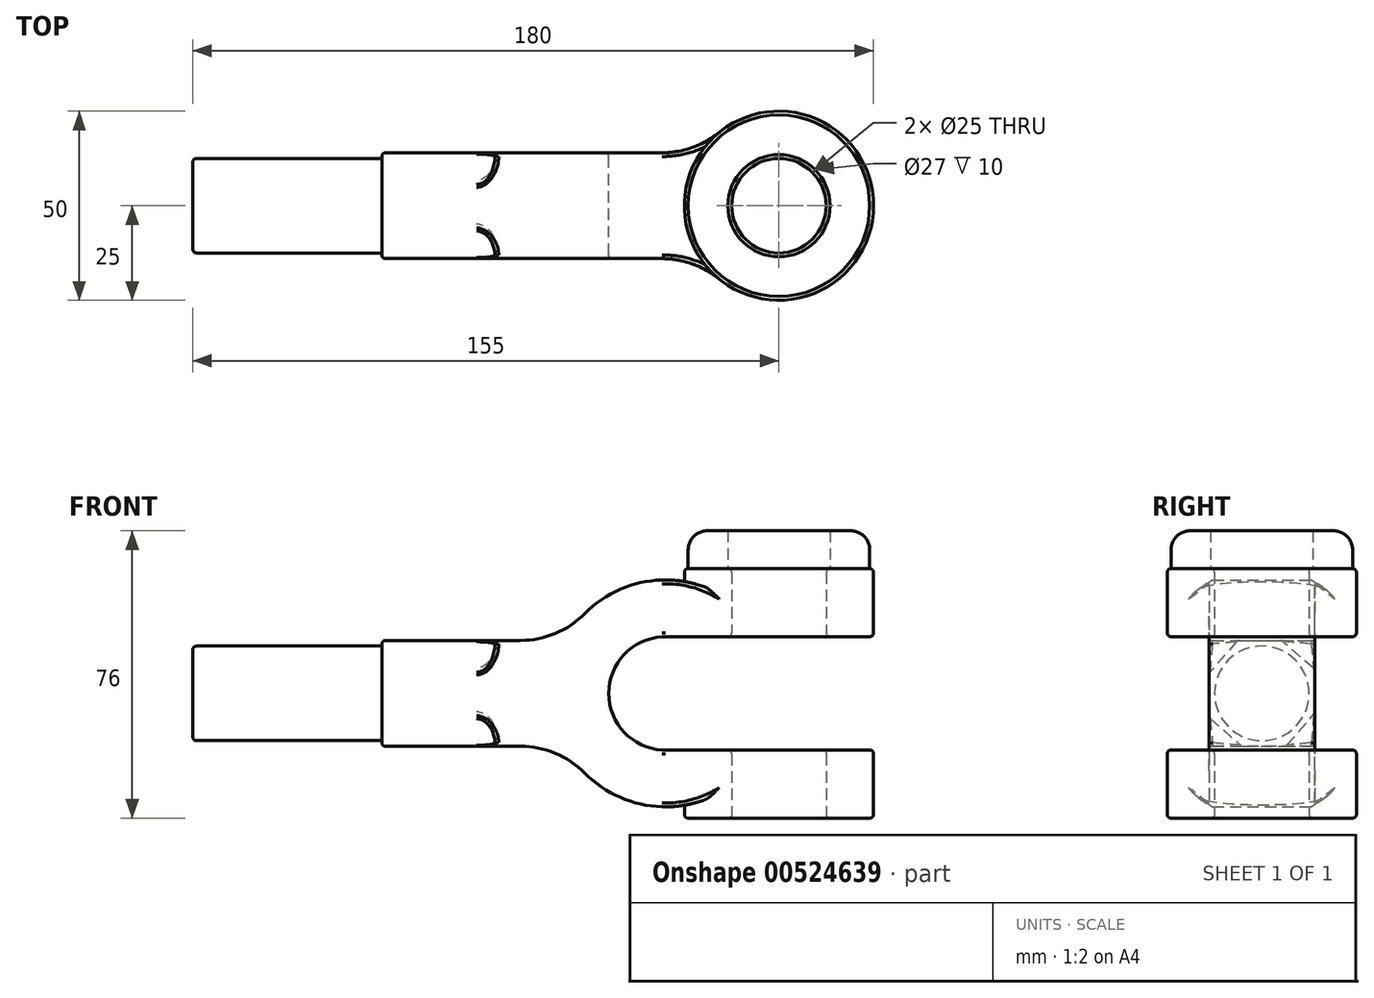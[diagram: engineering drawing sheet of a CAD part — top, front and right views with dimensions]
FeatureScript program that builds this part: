
annotation { "Feature Type Name" : "Feature", "Feature Type Description" : "" }
export const myFeature = defineFeature(function(context is Context, id is Id, definition is map)
    precondition{}
    {
        {
            var Q0;
            Q0=qCreatedBy(makeId("Top.planeOp"),FACE);
            var sketch = newSketch(context, id + "F0", { "sketchPlane" : qUnion([Q0])});
            skCircle(sketch, "E0", {"center": v(0, 0) * mm, "radius": 25 * mm});
            skSolve(sketch);
        }
        {
            var Q0;
            Q0=qSketchRegion(id+"F0",true);
            extrude(context, id + "F1", {"entities" : qUnion([Q0]), "endBound" : BoundingType.SYMMETRIC, "depth" : 66 * mm, "offsetDistance" : 25 * mm});
        }
        {
            var Q0;
            Q0=qCreatedBy(makeId("Front.planeOp"),FACE);
            var sketch = newSketch(context, id + "F2", { "sketchPlane" : qUnion([Q0])});
            skArc(sketch, "E1", {"start": v(-56.53, -14) * mm, "mid": v(0, 0) * mm, "end": v(-56.53, 14) * mm});
            skCircle(sketch, "E2", {"center": v(-30, 0) * mm, "radius": 15 * mm});
            skLineSegment(sketch, "E3.bottom", {"start": v(-75, 14) * mm, "end": v(-65, 14) * mm});
            skLineSegment(sketch, "E3.top", {"start": v(-75, -14) * mm, "end": v(-56.53, -14) * mm});
            skLineSegment(sketch, "E3.left", {"start": v(-75, 14) * mm, "end": v(-75, -14) * mm});
            skLineSegment(sketch, "E4", {"start": v(-65, 14) * mm, "end": v(-56.53, 14) * mm});
            skPoint(sketch, "E5.orphan", {"position": v(-55, 14) * mm});
            skSolve(sketch);
        }
        {
            var Q0;
            Q0=qSketchRegion(id+"F2",true);
            extrude(context, id + "F3", {"entities" : qUnion([Q0]), "operationType" : NewBodyOperationType.ADD, "endBound" : BoundingType.SYMMETRIC, "depth" : 28 * mm, "offsetDistance" : 25 * mm});
        }
        {
            var Q0;
            Q0=makeQuery(id+"F3.opExtrude","SWEPT_FACE",FACE,{"disambiguationData":[OSD([sQuery(id+"F2.wireOp",EDGE,"E3.left")])]});
            extrude(context, id + "F4", {"entities" : qUnion([Q0]), "operationType" : NewBodyOperationType.ADD, "depth" : 30 * mm, "offsetDistance" : 25 * mm});
        }
        {
            var Q0;
            Q0=makeQuery(id+"F4.opExtrude","CAP_FACE",FACE,{"disambiguationData":[OSD([sQuery(id+"F2.wireOp",EDGE,"E3.left")])],"isStart":false});
            var sketch = newSketch(context, id + "F5", { "sketchPlane" : qUnion([Q0])});
            skCircle(sketch, "E6", {"center": v(0, 0) * mm, "radius": 12.5 * mm});
            skSolve(sketch);
        }
        {
            var Q0;
            Q0=qSketchRegion(id+"F5",true);
            extrude(context, id + "F6", {"entities" : qUnion([Q0]), "operationType" : NewBodyOperationType.ADD, "depth" : 50 * mm, "offsetDistance" : 25 * mm});
        }
        {
            var Q0;
            Q0=qCreatedBy(makeId("Front.planeOp"),FACE);
            var sketch = newSketch(context, id + "F7", { "sketchPlane" : qUnion([Q0])});
            skLineSegment(sketch, "E7.bottom", {"start": v(-30, 15) * mm, "end": v(30, 15) * mm});
            skLineSegment(sketch, "E7.top", {"start": v(-30, -15) * mm, "end": v(30, -15) * mm});
            skLineSegment(sketch, "E7.left", {"start": v(-30, 15) * mm, "end": v(-30, -15) * mm});
            skLineSegment(sketch, "E7.right", {"start": v(30, 15) * mm, "end": v(30, -15) * mm});
            skPoint(sketch, "E7.middle", {"position": v(0, 0) * mm});
            skSolve(sketch);
        }
        {
            var Q0;
            Q0=qSketchRegion(id+"F7",true);
            extrude(context, id + "F8", {"entities" : qUnion([Q0]), "operationType" : NewBodyOperationType.REMOVE, "endBound" : BoundingType.SYMMETRIC, "oppositeDirection" : true, "depth" : 60 * mm, "offsetDistance" : 25 * mm});
        }
        {
            var Q0;
            Q0=makeQuery(id+"F1.opExtrude","CAP_FACE",FACE,{"disambiguationData":[OSD([sQuery(id+"F0.wireOp",EDGE,"E0")])],"isStart":true});
            var sketch = newSketch(context, id + "F9", { "sketchPlane" : qUnion([Q0])});
            skCircle(sketch, "E8", {"center": v(0, 0) * mm, "radius": 12.5 * mm});
            skSolve(sketch);
        }
        {
            var Q0;
            Q0=qSketchRegion(id+"F9",true);
            extrude(context, id + "F10", {"entities" : qUnion([Q0]), "operationType" : NewBodyOperationType.REMOVE, "endBound" : BoundingType.THROUGH_ALL, "oppositeDirection" : true, "depth" : 25 * mm, "offsetDistance" : 25 * mm});
        }
        {
            var Q0;
            Q0=makeQuery(id+"F3.boolean.opBoolean","INTERSECT",EDGE,{"disambiguationData":[OD(1.0)],"derivedFrom":[makeQuery(id+"F1.opExtrude","SWEPT_FACE",FACE,{"disambiguationData":[OSD([sQuery(id+"F0.wireOp",EDGE,"E0")])]}),makeQuery(id+"F3.opExtrude","CAP_FACE",FACE,{"disambiguationData":[OSD([sQuery(id+"F2.wireOp",EDGE,"E1"),sQuery(id+"F2.wireOp",EDGE,"E2"),sQuery(id+"F2.wireOp",EDGE,"E3.bottom"),sQuery(id+"F2.wireOp",EDGE,"E3.top"),sQuery(id+"F2.wireOp",EDGE,"E3.left"),sQuery(id+"F2.wireOp",EDGE,"E4")])],"isStart":false})]});
            fillet(context, id + "F11", {"entities" : qUnion([Q0]), "radius" : 24 * mm, "tangentPropagation" : true, "allowEdgeOverflow" : false});
        }
        {
            var Q0;
            Q0=makeQuery(id+"F3.boolean.opBoolean","INTERSECT",EDGE,{"disambiguationData":[OD(0.0)],"derivedFrom":[makeQuery(id+"F1.opExtrude","SWEPT_FACE",FACE,{"disambiguationData":[OSD([sQuery(id+"F0.wireOp",EDGE,"E0")])]}),makeQuery(id+"F3.opExtrude","CAP_FACE",FACE,{"disambiguationData":[OSD([sQuery(id+"F2.wireOp",EDGE,"E1"),sQuery(id+"F2.wireOp",EDGE,"E2"),sQuery(id+"F2.wireOp",EDGE,"E3.bottom"),sQuery(id+"F2.wireOp",EDGE,"E3.top"),sQuery(id+"F2.wireOp",EDGE,"E3.left"),sQuery(id+"F2.wireOp",EDGE,"E4")])],"isStart":false})]});
            fillet(context, id + "F12", {"entities" : qUnion([Q0]), "radius" : 24 * mm, "tangentPropagation" : true, "allowEdgeOverflow" : false});
        }
        {
            var Q0;
            Q0=makeQuery(id+"F3.boolean.opBoolean","INTERSECT",EDGE,{"disambiguationData":[OD(0.0)],"derivedFrom":[makeQuery(id+"F1.opExtrude","SWEPT_FACE",FACE,{"disambiguationData":[OSD([sQuery(id+"F0.wireOp",EDGE,"E0")])]}),makeQuery(id+"F3.opExtrude","CAP_FACE",FACE,{"disambiguationData":[OSD([sQuery(id+"F2.wireOp",EDGE,"E1"),sQuery(id+"F2.wireOp",EDGE,"E2"),sQuery(id+"F2.wireOp",EDGE,"E3.bottom"),sQuery(id+"F2.wireOp",EDGE,"E3.top"),sQuery(id+"F2.wireOp",EDGE,"E3.left"),sQuery(id+"F2.wireOp",EDGE,"E4")])],"isStart":true})]});
            fillet(context, id + "F13", {"entities" : qUnion([Q0]), "radius" : 24 * mm, "tangentPropagation" : true, "allowEdgeOverflow" : false});
        }
        {
            var Q0;
            Q0=makeQuery(id+"F3.boolean.opBoolean","INTERSECT",EDGE,{"disambiguationData":[OD(1.0)],"derivedFrom":[makeQuery(id+"F1.opExtrude","SWEPT_FACE",FACE,{"disambiguationData":[OSD([sQuery(id+"F0.wireOp",EDGE,"E0")])]}),makeQuery(id+"F3.opExtrude","CAP_FACE",FACE,{"disambiguationData":[OSD([sQuery(id+"F2.wireOp",EDGE,"E1"),sQuery(id+"F2.wireOp",EDGE,"E2"),sQuery(id+"F2.wireOp",EDGE,"E3.bottom"),sQuery(id+"F2.wireOp",EDGE,"E3.top"),sQuery(id+"F2.wireOp",EDGE,"E3.left"),sQuery(id+"F2.wireOp",EDGE,"E4")])],"isStart":true})]});
            fillet(context, id + "F14", {"entities" : qUnion([Q0]), "radius" : 24 * mm, "tangentPropagation" : true, "allowEdgeOverflow" : false});
        }
        {
            var Q0;
            Q0=makeQuery(id+"F3.opExtrude","SWEPT_EDGE",EDGE,{"disambiguationData":[OSD([sQuery(id+"F2.wireOp",EDGE,"E1"),sQuery(id+"F2.wireOp",EDGE,"E3.top")])]});
            fillet(context, id + "F15", {"entities" : qUnion([Q0]), "radius" : 24 * mm, "tangentPropagation" : true, "allowEdgeOverflow" : false});
        }
        {
            var Q0;
            Q0=makeQuery(id+"F3.opExtrude","SWEPT_EDGE",EDGE,{"disambiguationData":[OSD([sQuery(id+"F2.wireOp",EDGE,"E1"),sQuery(id+"F2.wireOp",EDGE,"E4")])]});
            fillet(context, id + "F16", {"entities" : qUnion([Q0]), "radius" : 24 * mm, "tangentPropagation" : true, "allowEdgeOverflow" : false});
        }
        {
            var Q0;
            Q0=makeQuery(id+"F4.opExtrude","CAP_FACE",FACE,{"disambiguationData":[OSD([sQuery(id+"F2.wireOp",EDGE,"E3.left")])],"isStart":false});
            var sketch = newSketch(context, id + "F17", { "sketchPlane" : qUnion([Q0])});
            skLineSegment(sketch, "E9", {"start": v(5.24, -14) * mm, "end": v(-6.37, -14) * mm});
            skLineSegment(sketch, "E10", {"start": v(-6.37, -14) * mm, "end": v(-14, -5.24) * mm});
            skLineSegment(sketch, "E11", {"start": v(-14, -5.24) * mm, "end": v(-14, 6.37) * mm});
            skLineSegment(sketch, "E12", {"start": v(-14, 6.37) * mm, "end": v(-5.24, 14) * mm});
            skLineSegment(sketch, "E13", {"start": v(-5.24, 14) * mm, "end": v(6.37, 14) * mm});
            skLineSegment(sketch, "E14", {"start": v(6.37, 14) * mm, "end": v(14, 5.24) * mm});
            skLineSegment(sketch, "E15", {"start": v(14, 5.24) * mm, "end": v(14, -6.37) * mm});
            skLineSegment(sketch, "E16", {"start": v(14, -6.37) * mm, "end": v(5.24, -14) * mm});
            skLineSegment(sketch, "E17.bottom", {"start": v(-18.8, -19.26) * mm, "end": v(18.8, -19.26) * mm});
            skLineSegment(sketch, "E17.top", {"start": v(-18.8, 19.26) * mm, "end": v(18.8, 19.26) * mm});
            skLineSegment(sketch, "E17.left", {"start": v(-18.8, -19.26) * mm, "end": v(-18.8, 19.26) * mm});
            skLineSegment(sketch, "E17.right", {"start": v(18.8, -19.26) * mm, "end": v(18.8, 19.26) * mm});
            skPoint(sketch, "E17.middle", {"position": v(0, 0) * mm});
            skSolve(sketch);
        }
        {
            var Q0;
            Q0=qSketchRegion(id+"F17",true);
            extrude(context, id + "F18", {"entities" : qUnion([Q0]), "operationType" : NewBodyOperationType.REMOVE, "oppositeDirection" : true, "depth" : 30 * mm, "offsetDistance" : 25 * mm});
        }
        {
            var Q0;
            Q0=makeQuery(id+"F18.boolean.opBoolean","COPY",EDGE,{"derivedFrom":makeQuery(id+"F18.opExtrude","CAP_EDGE",EDGE,{"disambiguationData":[OSD([sQuery(id+"F17.wireOp",EDGE,"E16")])],"isStart":false})});
            fillet(context, id + "F19", {"entities" : qUnion([Q0]), "radius" : 5 * mm, "tangentPropagation" : true, "allowEdgeOverflow" : false});
        }
        {
            var Q0;
            Q0=makeQuery(id+"F18.boolean.opBoolean","COPY",EDGE,{"derivedFrom":makeQuery(id+"F18.opExtrude","CAP_EDGE",EDGE,{"disambiguationData":[OSD([sQuery(id+"F17.wireOp",EDGE,"E10")])],"isStart":false})});
            fillet(context, id + "F20", {"entities" : qUnion([Q0]), "radius" : 5 * mm, "tangentPropagation" : true, "allowEdgeOverflow" : false});
        }
        {
            var Q0;
            Q0=makeQuery(id+"F18.boolean.opBoolean","COPY",EDGE,{"derivedFrom":makeQuery(id+"F18.opExtrude","CAP_EDGE",EDGE,{"disambiguationData":[OSD([sQuery(id+"F17.wireOp",EDGE,"E12")])],"isStart":false})});
            fillet(context, id + "F21", {"entities" : qUnion([Q0]), "radius" : 5 * mm, "tangentPropagation" : true, "allowEdgeOverflow" : false});
        }
        {
            var Q0;
            Q0=makeQuery(id+"F18.boolean.opBoolean","COPY",EDGE,{"derivedFrom":makeQuery(id+"F18.opExtrude","CAP_EDGE",EDGE,{"disambiguationData":[OSD([sQuery(id+"F17.wireOp",EDGE,"E14")])],"isStart":false})});
            fillet(context, id + "F22", {"entities" : qUnion([Q0]), "radius" : 5 * mm, "tangentPropagation" : true, "allowEdgeOverflow" : false});
        }
        {
            var Q0;
            {var subQ0=sQuery(id+"F2.wireOp",EDGE,"E3.left");Q0=makeQuery(id+"F4.boolean.opBoolean","MERGE",FACE,{"derivedFrom":[makeQuery(id+"F3.opExtrude","CAP_FACE",FACE,{"disambiguationData":[OSD([sQuery(id+"F2.wireOp",EDGE,"E1"),sQuery(id+"F2.wireOp",EDGE,"E2"),sQuery(id+"F2.wireOp",EDGE,"E3.bottom"),sQuery(id+"F2.wireOp",EDGE,"E3.top"),subQ0,sQuery(id+"F2.wireOp",EDGE,"E4")])],"isStart":false}),makeQuery(id+"F4.opExtrude","SWEPT_FACE",FACE,{"disambiguationData":[OSD([subQ0]),TDD([makeQuery(id+"F3.opExtrude","CAP_EDGE",EDGE,{"disambiguationData":[OSD([subQ0])],"isStart":false})])]})]});}
            var Q1;
            {var subQ0=sQuery(id+"F2.wireOp",EDGE,"E3.top");Q1=makeQuery(id+"F4.boolean.opBoolean","MERGE",FACE,{"derivedFrom":[makeQuery(id+"F3.opExtrude","SWEPT_FACE",FACE,{"disambiguationData":[OSD([subQ0])]}),makeQuery(id+"F4.opExtrude","SWEPT_FACE",FACE,{"disambiguationData":[OSD([subQ0,sQuery(id+"F2.wireOp",EDGE,"E3.left")])]})]});}
            var Q2;
            {var subQ0=sQuery(id+"F2.wireOp",EDGE,"E3.left");Q2=makeQuery(id+"F4.boolean.opBoolean","MERGE",FACE,{"derivedFrom":[makeQuery(id+"F3.opExtrude","CAP_FACE",FACE,{"disambiguationData":[OSD([sQuery(id+"F2.wireOp",EDGE,"E1"),sQuery(id+"F2.wireOp",EDGE,"E2"),sQuery(id+"F2.wireOp",EDGE,"E3.bottom"),sQuery(id+"F2.wireOp",EDGE,"E3.top"),subQ0,sQuery(id+"F2.wireOp",EDGE,"E4")])],"isStart":true}),makeQuery(id+"F4.opExtrude","SWEPT_FACE",FACE,{"disambiguationData":[OSD([subQ0]),TDD([makeQuery(id+"F3.opExtrude","CAP_EDGE",EDGE,{"disambiguationData":[OSD([subQ0])],"isStart":true})])]})]});}
            var Q3;
            {var subQ0=sQuery(id+"F2.wireOp",EDGE,"E3.bottom");Q3=makeQuery(id+"F4.boolean.opBoolean","MERGE",FACE,{"derivedFrom":[makeQuery(id+"F3.opExtrude","SWEPT_FACE",FACE,{"disambiguationData":[OSD([subQ0,sQuery(id+"F2.wireOp",EDGE,"E4")])]}),makeQuery(id+"F4.opExtrude","SWEPT_FACE",FACE,{"disambiguationData":[OSD([subQ0,sQuery(id+"F2.wireOp",EDGE,"E3.left")])]})]});}
            var Q4;
            Q4=makeQuery(id+"F1.opExtrude","CAP_FACE",FACE,{"disambiguationData":[OSD([sQuery(id+"F0.wireOp",EDGE,"E0")])],"isStart":false});
            var Q5;
            Q5=makeQuery(id+"F1.opExtrude","CAP_FACE",FACE,{"disambiguationData":[OSD([sQuery(id+"F0.wireOp",EDGE,"E0")])],"isStart":true});
            var Q6;
            Q6=makeQuery(id+"F8.boolean.opBoolean","COPY",FACE,{"derivedFrom":makeQuery(id+"F8.opExtrude","SWEPT_FACE",FACE,{"disambiguationData":[OSD([sQuery(id+"F7.wireOp",EDGE,"E7.bottom")])]})});
            var Q7;
            Q7=makeQuery(id+"F8.boolean.opBoolean","COPY",FACE,{"derivedFrom":makeQuery(id+"F8.opExtrude","SWEPT_FACE",FACE,{"disambiguationData":[OSD([sQuery(id+"F7.wireOp",EDGE,"E7.top")])]})});
            var Q8;
            Q8=makeQuery(id+"F18.boolean.opBoolean","COPY",FACE,{"derivedFrom":makeQuery(id+"F18.opExtrude","SWEPT_FACE",FACE,{"disambiguationData":[OSD([sQuery(id+"F17.wireOp",EDGE,"E16")])]})});
            var Q9;
            Q9=makeQuery(id+"F18.boolean.opBoolean","COPY",FACE,{"derivedFrom":makeQuery(id+"F18.opExtrude","SWEPT_FACE",FACE,{"disambiguationData":[OSD([sQuery(id+"F17.wireOp",EDGE,"E10")])]})});
            var Q10;
            Q10=makeQuery(id+"F18.boolean.opBoolean","COPY",FACE,{"derivedFrom":makeQuery(id+"F18.opExtrude","SWEPT_FACE",FACE,{"disambiguationData":[OSD([sQuery(id+"F17.wireOp",EDGE,"E12")])]})});
            var Q11;
            Q11=makeQuery(id+"F18.boolean.opBoolean","COPY",FACE,{"derivedFrom":makeQuery(id+"F18.opExtrude","SWEPT_FACE",FACE,{"disambiguationData":[OSD([sQuery(id+"F17.wireOp",EDGE,"E14")])]})});
            var Q12;
            Q12=makeQuery(id+"F6.opExtrude","CAP_FACE",FACE,{"disambiguationData":[OSD([sQuery(id+"F5.wireOp",EDGE,"E6")])],"isStart":false});
            fillet(context, id + "F23", {"entities" : qUnion([Q0, Q1, Q2, Q3, Q4, Q5, Q6, Q7, Q8, Q9, Q10, Q11, Q12]), "radius" : 1 * mm, "tangentPropagation" : true, "allowEdgeOverflow" : false});
        }
        {
            var Q0;
            Q0=makeQuery(id+"F1.opExtrude","CAP_FACE",FACE,{"disambiguationData":[OSD([sQuery(id+"F0.wireOp",EDGE,"E0")])],"isStart":false});
            extrude(context, id + "F24", {"entities" : qUnion([Q0]), "operationType" : NewBodyOperationType.ADD, "depth" : 10 * mm, "offsetDistance" : 25 * mm});
        }
        {
            var Q0;
            Q0=makeQuery(id+"F24.opExtrude","CAP_EDGE",EDGE,{"disambiguationData":[OSD([sQuery(id+"F0.wireOp",EDGE,"E0")])],"isStart":false});
            fillet(context, id + "F25", {"entities" : qUnion([Q0]), "radius" : 5 * mm, "tangentPropagation" : true, "allowEdgeOverflow" : false});
        }
    });
